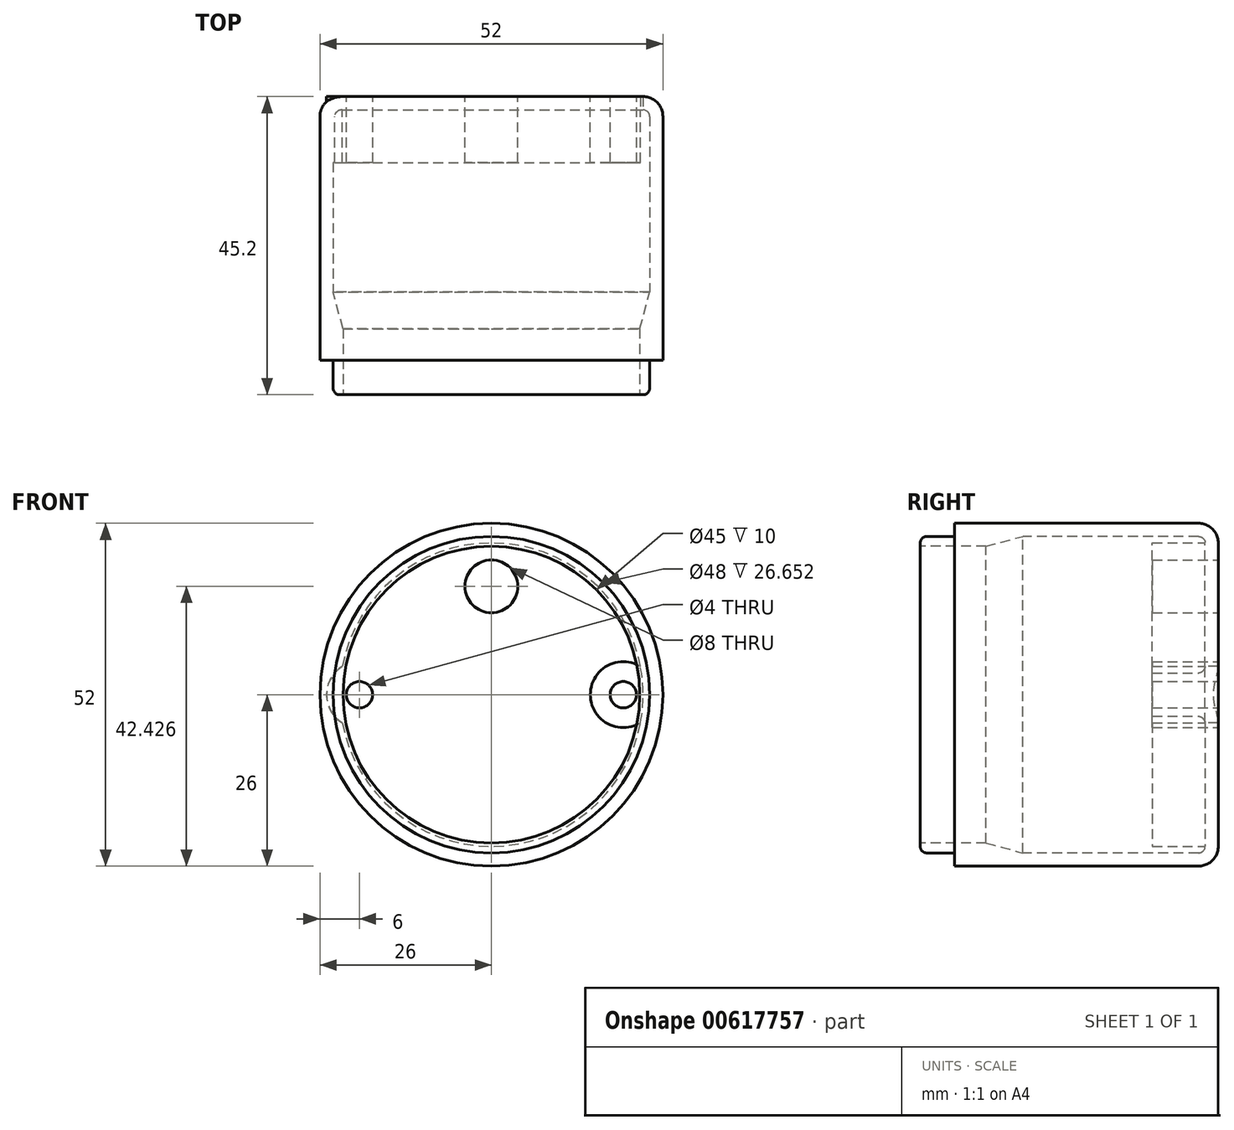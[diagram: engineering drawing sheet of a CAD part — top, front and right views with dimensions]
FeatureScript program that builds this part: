
annotation { "Feature Type Name" : "Feature", "Feature Type Description" : "" }
export const myFeature = defineFeature(function(context is Context, id is Id, definition is map)
    precondition{}
    {
        {
            var Q0;
            Q0=qCreatedBy(makeId("Right.planeOp"),FACE);
            var sketch = newSketch(context, id + "F0", { "sketchPlane" : qUnion([Q0])});
            skLineSegment(sketch, "E0.bottom", {"start": v(0, 0) * mm, "end": v(-2, 0) * mm});
            skLineSegment(sketch, "E0.top", {"start": v(-3, 26) * mm, "end": v(-40, 26) * mm});
            skLineSegment(sketch, "E0.left", {"start": v(0, 0) * mm, "end": v(0, 23) * mm});
            skPoint(sketch, "E1.visualSharp", {"position": v(0, 26) * mm});
            skArc(sketch, "E1.filletArc", {"start": v(0, 23) * mm, "mid": v(-0.88, 25.12) * mm, "end": v(-3, 26) * mm});
            skLineSegment(sketch, "E2.0", {"start": v(-3, 24) * mm, "end": v(-29.65, 24) * mm});
            skArc(sketch, "E2.1", {"start": v(-2, 23) * mm, "mid": v(-2.3, 23.7) * mm, "end": v(-3, 24) * mm});
            skLineSegment(sketch, "E2.2", {"start": v(-2, 0) * mm, "end": v(-2, 23) * mm});
            skLineSegment(sketch, "E3.bottom", {"start": v(-40, 24) * mm, "end": v(-44.2, 24) * mm});
            skLineSegment(sketch, "E3.top", {"start": v(-35.2, 22.5) * mm, "end": v(-45.2, 22.5) * mm});
            skLineSegment(sketch, "E3.right", {"start": v(-45.2, 23) * mm, "end": v(-45.2, 22.5) * mm});
            skLineSegment(sketch, "E4.trimOffspring", {"start": v(-40, 24) * mm, "end": v(-40, 26) * mm});
            skPoint(sketch, "E5.visualSharp", {"position": v(-45.2, 24) * mm});
            skArc(sketch, "E5.filletArc", {"start": v(-44.2, 24) * mm, "mid": v(-44.91, 23.7) * mm, "end": v(-45.2, 23) * mm});
            skLineSegment(sketch, "E6", {"start": v(-61.31, 0) * mm, "end": v(23.73, 0) * mm, "construction": true});
            skLineSegment(sketch, "E7", {"start": v(-35.2, 22.5) * mm, "end": v(-29.65, 24) * mm});
            skSolve(sketch);
        }
        {
            var Q0;
            Q0 = qSketchRegion(id + "F0", true);
            var Q1;
            Q1=sQuery(id+"F0.wireOp",EDGE,"E6");
            revolve(context, id + "F1", {"surfaceOperationType" : NewSurfaceOperationType.NEW, "entities" : qUnion([Q0]), "axis" : qUnion([Q1]), "revolveType" : RevolveType.FULL});
        }
        {
            var Q0;
            Q0=makeQuery(id+"F1.opRevolve","SWEPT_FACE",FACE,{"disambiguationData":[OSD([sQuery(id+"F0.wireOp",EDGE,"E0.left")])]});
            var sketch = newSketch(context, id + "F2", { "sketchPlane" : qUnion([Q0])});
            skCircle(sketch, "E8", {"center": v(0, 0) * mm, "radius": 20 * mm, "construction": true});
            skLineSegment(sketch, "E9", {"start": v(0, 0) * mm, "end": v(58.63, 0) * mm, "construction": true});
            skCircle(sketch, "E10", {"center": v(20, 0) * mm, "radius": 2 * mm});
            skCircle(sketch, "E11", {"center": v(20, 0) * mm, "radius": 5 * mm});
            skLineSegment(sketch, "E12", {"start": v(0, 0) * mm, "end": v(0, 32.85) * mm, "construction": true});
            skCircle(sketch, "E13.MirrorC", {"center": v(-20, 0) * mm, "radius": 2 * mm});
            skCircle(sketch, "E14.MirrorC", {"center": v(-20, 0) * mm, "radius": 5 * mm});
            skCircle(sketch, "E15", {"center": v(0, 16.43) * mm, "radius": 4 * mm});
            skSolve(sketch);
        }
        {
            var Q0;
            {var subQ0=sQuery(id+"F2.wireOp",EDGE,"E11");var subQ1=makeQuery(id+"F1.opRevolve","SWEPT_EDGE",EDGE,{"disambiguationData":[OSD([sQuery(id+"F0.wireOp",EDGE,"E0.left"),sQuery(id+"F0.wireOp",EDGE,"E1.filletArc")])]});var subQ2=makeQuery(id+"F2.imprint","INTERSECT",VERTEX,{"disambiguationData":[OD(0.0)],"derivedFrom":[subQ1,subQ0]});Q0=makeQuery(id+"F2.imprint","IMPRINT",FACE,{"disambiguationData":[TD([[makeQuery(id+"F2.imprint","IMPRINT",EDGE,{"disambiguationData":[TD([[subQ2,-1.0]])],"derivedFrom":subQ0}),1.0]])]});}
            var Q1;
            Q1=makeQuery(id+"F2.imprint","IMPRINT",FACE,{"disambiguationData":[TD([[makeQuery(id+"F2.imprint","IMPRINT",EDGE,{"derivedFrom":sQuery(id+"F2.wireOp",EDGE,"E10")}),-1.0]])]});
            var Q2;
            Q2=makeQuery(id+"F2.imprint","IMPRINT",FACE,{"disambiguationData":[TD([[makeQuery(id+"F2.imprint","IMPRINT",EDGE,{"derivedFrom":sQuery(id+"F2.wireOp",EDGE,"E13.MirrorC")}),1.0]])]});
            var Q3;
            {var subQ0=sQuery(id+"F2.wireOp",EDGE,"E14.MirrorC");var subQ1=makeQuery(id+"F1.opRevolve","SWEPT_EDGE",EDGE,{"disambiguationData":[OSD([sQuery(id+"F0.wireOp",EDGE,"E0.left"),sQuery(id+"F0.wireOp",EDGE,"E1.filletArc")])]});var subQ2=makeQuery(id+"F2.imprint","INTERSECT",VERTEX,{"disambiguationData":[OD(0.0)],"derivedFrom":[subQ1,subQ0]});Q3=makeQuery(id+"F2.imprint","IMPRINT",FACE,{"disambiguationData":[TD([[makeQuery(id+"F2.imprint","IMPRINT",EDGE,{"disambiguationData":[TD([[subQ2,-1.0]])],"derivedFrom":subQ0}),-1.0]])]});}
            extrude(context, id + "F3", {"entities" : qUnion([Q0, Q1, Q2, Q3]), "operationType" : NewBodyOperationType.ADD, "oppositeDirection" : true, "depth" : 10 * mm, "offsetDistance" : 25 * mm});
        }
        {
            var Q0;
            Q0=makeQuery(id+"F3.boolean.opBoolean","SPLIT",FACE,{"disambiguationData":[TD([makeQuery(id+"F3.opExtrude","SWEPT_FACE",FACE,{"disambiguationData":[OSD([sQuery(id+"F2.wireOp",EDGE,"E10")])]})])],"derivedFrom":makeQuery(id+"F1.opRevolve","SWEPT_FACE",FACE,{"disambiguationData":[OSD([sQuery(id+"F0.wireOp",EDGE,"E2.2")])]})});
            var Q1;
            Q1=makeQuery(id+"F3.boolean.opBoolean","SPLIT",FACE,{"disambiguationData":[TD([makeQuery(id+"F3.opExtrude","SWEPT_FACE",FACE,{"disambiguationData":[OSD([sQuery(id+"F2.wireOp",EDGE,"E13.MirrorC")])]})])],"derivedFrom":makeQuery(id+"F1.opRevolve","SWEPT_FACE",FACE,{"disambiguationData":[OSD([sQuery(id+"F0.wireOp",EDGE,"E2.2")])]})});
            var Q2;
            Q2 = qSketchRegion(id + "F2", true);
            var Q3;
            Q3=makeQuery(id+"F3.boolean.opBoolean","MERGE",FACE,{"derivedFrom":[makeQuery(id+"F1.opRevolve","SWEPT_FACE",FACE,{"disambiguationData":[OSD([sQuery(id+"F0.wireOp",EDGE,"E0.left")])]}),makeQuery(id+"F3.opExtrude","CAP_FACE",FACE,{"disambiguationData":[OSD([sQuery(id+"F2.wireOp",EDGE,"E10"),sQuery(id+"F2.wireOp",EDGE,"E11")])],"isStart":true}),makeQuery(id+"F3.opExtrude","CAP_FACE",FACE,{"disambiguationData":[OSD([sQuery(id+"F2.wireOp",EDGE,"E13.MirrorC"),sQuery(id+"F2.wireOp",EDGE,"E14.MirrorC")])],"isStart":true})]});
            extrude(context, id + "F4", {"entities" : qUnion([Q0, Q1, Q2, Q3]), "operationType" : NewBodyOperationType.REMOVE, "oppositeDirection" : true, "depth" : 7.6 * mm, "offsetDistance" : 25 * mm});
        }
        {
            var Q0;
            Q0=makeQuery(id+"F2.imprint","IMPRINT",FACE,{"disambiguationData":[TD([[makeQuery(id+"F2.imprint","IMPRINT",EDGE,{"derivedFrom":sQuery(id+"F2.wireOp",EDGE,"E15")}),1.0]])]});
            extrude(context, id + "F5", {"entities" : qUnion([Q0]), "operationType" : NewBodyOperationType.REMOVE, "oppositeDirection" : true, "depth" : 25 * mm, "offsetDistance" : 25 * mm});
        }
    });
